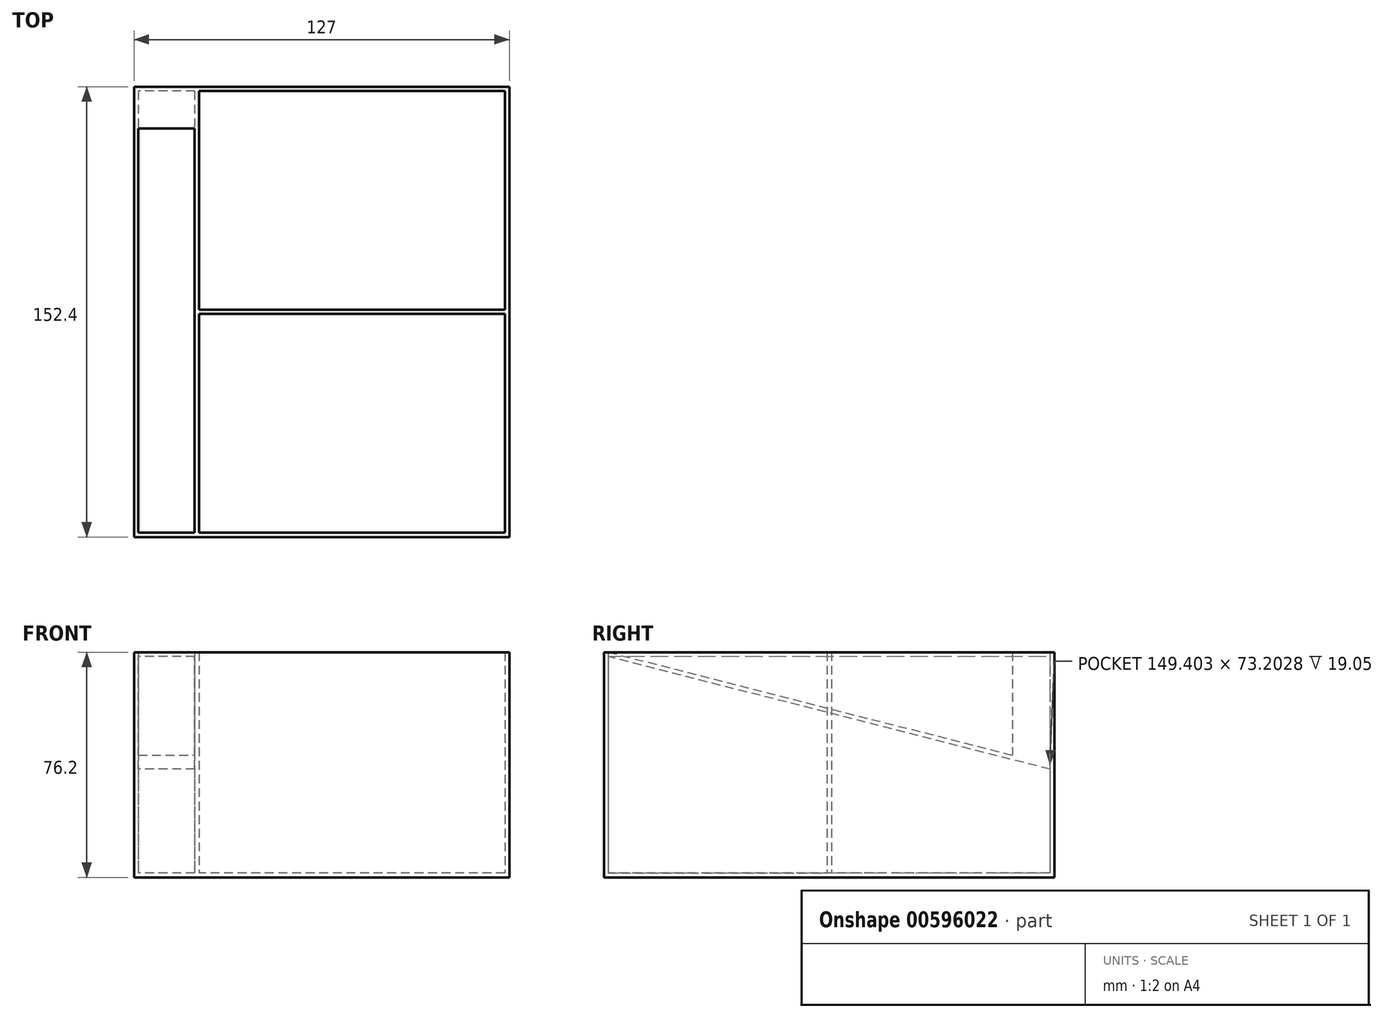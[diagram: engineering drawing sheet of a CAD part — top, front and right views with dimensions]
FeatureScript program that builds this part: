
annotation { "Feature Type Name" : "Feature", "Feature Type Description" : "" }
export const myFeature = defineFeature(function(context is Context, id is Id, definition is map)
    precondition{}
    {
        {
            var Q0;
            Q0=qCreatedBy(makeId("Top.planeOp"),FACE);
            var sketch = newSketch(context, id + "F0", { "sketchPlane" : qUnion([Q0])});
            skLineSegment(sketch, "E0.bottom", {"start": v(63.5, -76.2) * mm, "end": v(-63.5, -76.2) * mm});
            skLineSegment(sketch, "E0.top", {"start": v(63.5, 76.2) * mm, "end": v(-63.5, 76.2) * mm});
            skLineSegment(sketch, "E0.left", {"start": v(63.5, -76.2) * mm, "end": v(63.5, 76.2) * mm});
            skLineSegment(sketch, "E0.right", {"start": v(-63.5, -76.2) * mm, "end": v(-63.5, 76.2) * mm});
            skPoint(sketch, "E0.middle", {"position": v(0, 0) * mm});
            skSolve(sketch);
        }
        {
            var Q0;
            Q0=makeQuery(id+"F0.imprint","IMPRINT",FACE,{"disambiguationData":[TD([[makeQuery(id+"F0.imprint","IMPRINT",EDGE,{"derivedFrom":sQuery(id+"F0.wireOp",EDGE,"E0.bottom")}),-1.0]])]});
            extrude(context, id + "F1", {"entities" : qUnion([Q0]), "depth" : 76.2 * mm, "offsetDistance" : 25.4 * mm});
        }
        {
            var Q0;
            Q0=makeQuery(id+"F1.opExtrude","CAP_FACE",FACE,{"disambiguationData":[OSD([sQuery(id+"F0.wireOp",EDGE,"E0.bottom"),sQuery(id+"F0.wireOp",EDGE,"E0.top"),sQuery(id+"F0.wireOp",EDGE,"E0.left"),sQuery(id+"F0.wireOp",EDGE,"E0.right")])],"isStart":false});
            shell(context, id + "F2", {"entities" : qUnion([Q0]), "thickness" : 1.5 * mm});
        }
        {
            var Q0;
            Q0=makeQuery(id+"F2.opShell","OFFSET_FACE",FACE,{"disambiguationData":[OSD([sQuery(id+"F0.wireOp",EDGE,"E0.bottom"),sQuery(id+"F0.wireOp",EDGE,"E0.top"),sQuery(id+"F0.wireOp",EDGE,"E0.left"),sQuery(id+"F0.wireOp",EDGE,"E0.right")])]});
            var sketch = newSketch(context, id + "F3", { "sketchPlane" : qUnion([Q0])});
            skLineSegment(sketch, "E1.bottom", {"start": v(-42.95, 74.7) * mm, "end": v(-41.45, 74.7) * mm});
            skLineSegment(sketch, "E1.top", {"start": v(-42.95, -74.7) * mm, "end": v(-41.45, -74.7) * mm});
            skLineSegment(sketch, "E1.left", {"start": v(-42.95, 74.7) * mm, "end": v(-42.95, -74.7) * mm});
            skLineSegment(sketch, "E1.right", {"start": v(-41.45, 74.7) * mm, "end": v(-41.45, -74.7) * mm});
            skSolve(sketch);
        }
        {
            var Q0;
            Q0=makeQuery(id+"F2.opShell","OFFSET_FACE",FACE,{"disambiguationData":[OSD([sQuery(id+"F0.wireOp",EDGE,"E0.right")])]});
            var sketch = newSketch(context, id + "F4", { "sketchPlane" : qUnion([Q0])});
            skLineSegment(sketch, "E2", {"start": v(74.7, 36.6) * mm, "end": v(-74.7, 74.7) * mm});
            skLineSegment(sketch, "E3", {"start": v(-74.7, 74.7) * mm, "end": v(-74.7, 76.2) * mm});
            skLineSegment(sketch, "E4", {"start": v(-74.7, 76.2) * mm, "end": v(74.7, 38.1) * mm});
            skLineSegment(sketch, "E5", {"start": v(74.7, 38.1) * mm, "end": v(74.7, 36.6) * mm});
            skSolve(sketch);
        }
        {
            var Q0;
            Q0 = qSketchRegion(id + "F3", true);
            var Q1;
            {var subQ0=sQuery(id+"F0.wireOp",EDGE,"E0.right");var subQ1=sQuery(id+"F0.wireOp",EDGE,"E0.top");Q1=makeQuery(id+"F2.opShell","OFFSET_VERTEX",VERTEX,{"disambiguationData":[OSD([subQ1,subQ0]),TDD([makeQuery(id+"F1.opExtrude","CAP_VERTEX",VERTEX,{"disambiguationData":[OSD([subQ1,subQ0])],"isStart":false})])]});}
            extrude(context, id + "F5", {"entities" : qUnion([Q0]), "operationType" : NewBodyOperationType.ADD, "endBound" : BoundingType.UP_TO_VERTEX, "depth" : 73.66 * mm, "endBoundEntityVertex" : qUnion([Q1]), "offsetDistance" : 25.4 * mm});
        }
        {
            var Q0;
            Q0 = qSketchRegion(id + "F4", true);
            var Q1;
            Q1=makeQuery(id+"F1.opExtrude","SWEPT_BODY",BODY,{"disambiguationData":[OSD([sQuery(id+"F0.wireOp",EDGE,"E0.bottom"),sQuery(id+"F0.wireOp",EDGE,"E0.top"),sQuery(id+"F0.wireOp",EDGE,"E0.left"),sQuery(id+"F0.wireOp",EDGE,"E0.right")])]});
            extrude(context, id + "F6", {"entities" : qUnion([Q0]), "operationType" : NewBodyOperationType.ADD, "endBound" : BoundingType.UP_TO_BODY, "depth" : 25.4 * mm, "endBoundEntityBody" : qUnion([Q1]), "offsetDistance" : 25.4 * mm});
        }
        {
            var Q0;
            {var subQ0=sQuery(id+"F0.wireOp",EDGE,"E0.top");Q0=makeQuery(id+"F6.boolean.opBoolean","SPLIT",FACE,{"disambiguationData":[TD([makeQuery(id+"F1.opExtrude","CAP_FACE",FACE,{"disambiguationData":[OSD([sQuery(id+"F0.wireOp",EDGE,"E0.bottom"),subQ0,sQuery(id+"F0.wireOp",EDGE,"E0.left"),sQuery(id+"F0.wireOp",EDGE,"E0.right")])],"isStart":false})])],"derivedFrom":makeQuery(id+"F5.opExtrude","SWEPT_FACE",FACE,{"disambiguationData":[OSD([sQuery(id+"F3.wireOp",EDGE,"E1.left")])]})});}
            var sketch = newSketch(context, id + "F7", { "sketchPlane" : qUnion([Q0])});
            skLineSegment(sketch, "E6", {"start": v(-74.7, 38.1) * mm, "end": v(-74.7, 76.2) * mm});
            skLineSegment(sketch, "E7", {"start": v(-74.7, 76.2) * mm, "end": v(-62, 76.2) * mm});
            skLineSegment(sketch, "E8", {"start": v(-62, 76.2) * mm, "end": v(-62, 41.34) * mm});
            skLineSegment(sketch, "E9", {"start": v(-62, 41.34) * mm, "end": v(-74.7, 38.1) * mm});
            skSolve(sketch);
        }
        {
            var Q0;
            Q0=makeQuery(id+"F7.imprint","IMPRINT",FACE,{"disambiguationData":[TD([[makeQuery(id+"F7.imprint","IMPRINT",EDGE,{"derivedFrom":sQuery(id+"F7.wireOp",EDGE,"E6")}),1.0]])]});
            var Q1;
            {var subQ0=sQuery(id+"F0.wireOp",EDGE,"E0.right");var subQ1=sQuery(id+"F0.wireOp",EDGE,"E0.top");Q1=makeQuery(id+"F6.boolean.opBoolean","SPLIT",FACE,{"disambiguationData":[TD([makeQuery(id+"F1.opExtrude","CAP_FACE",FACE,{"disambiguationData":[OSD([sQuery(id+"F0.wireOp",EDGE,"E0.bottom"),subQ1,sQuery(id+"F0.wireOp",EDGE,"E0.left"),subQ0])],"isStart":false})])],"derivedFrom":makeQuery(id+"F2.opShell","OFFSET_FACE",FACE,{"disambiguationData":[OSD([subQ0])]})});}
            extrude(context, id + "F8", {"entities" : qUnion([Q0]), "operationType" : NewBodyOperationType.ADD, "endBound" : BoundingType.UP_TO_SURFACE, "depth" : 25.4 * mm, "endBoundEntityFace" : qUnion([Q1]), "offsetDistance" : 25.4 * mm});
        }
        {
            var Q0;
            {var subQ0=sQuery(id+"F0.wireOp",EDGE,"E0.bottom");var subQ1=sQuery(id+"F0.wireOp",EDGE,"E0.top");var subQ2=sQuery(id+"F0.wireOp",EDGE,"E0.left");Q0=makeQuery(id+"F5.boolean.opBoolean","SPLIT",FACE,{"disambiguationData":[TD([makeQuery(id+"F2.opShell","OFFSET_FACE",FACE,{"disambiguationData":[OSD([subQ2])]})])],"derivedFrom":makeQuery(id+"F2.opShell","OFFSET_FACE",FACE,{"disambiguationData":[OSD([subQ0,subQ1,subQ2,sQuery(id+"F0.wireOp",EDGE,"E0.right")])]})});}
            var sketch = newSketch(context, id + "F9", { "sketchPlane" : qUnion([Q0])});
            skLineSegment(sketch, "E10", {"start": v(10.27, 74.7) * mm, "end": v(10.27, -74.7) * mm, "construction": true});
            skLineSegment(sketch, "E11", {"start": v(62, 0) * mm, "end": v(-41.45, 0) * mm, "construction": true});
            skLineSegment(sketch, "E12.bottom", {"start": v(62, -0.75) * mm, "end": v(-41.45, -0.75) * mm});
            skLineSegment(sketch, "E12.top", {"start": v(62, 0.75) * mm, "end": v(-41.45, 0.75) * mm});
            skLineSegment(sketch, "E12.left", {"start": v(62, -0.75) * mm, "end": v(62, 0.75) * mm});
            skLineSegment(sketch, "E12.right", {"start": v(-41.45, -0.75) * mm, "end": v(-41.45, 0.75) * mm});
            skPoint(sketch, "E12.middle", {"position": v(10.27, 0) * mm});
            skSolve(sketch);
        }
        {
            var Q0;
            Q0 = qSketchRegion(id + "F9", true);
            var Q1;
            Q1=makeQuery(id+"F1.opExtrude","SWEPT_BODY",BODY,{"disambiguationData":[OSD([sQuery(id+"F0.wireOp",EDGE,"E0.bottom"),sQuery(id+"F0.wireOp",EDGE,"E0.top"),sQuery(id+"F0.wireOp",EDGE,"E0.left"),sQuery(id+"F0.wireOp",EDGE,"E0.right")])]});
            var Q2;
            Q2=makeQuery(id+"F5.opExtrude","CAP_VERTEX",VERTEX,{"disambiguationData":[OSD([sQuery(id+"F0.wireOp",EDGE,"E0.bottom"),sQuery(id+"F3.wireOp",EDGE,"E1.top"),sQuery(id+"F3.wireOp",EDGE,"E1.right"),dummyQuery(id+"F5.vertexPlane.planeOp",FACE)])],"isStart":false});
            extrude(context, id + "F10", {"entities" : qUnion([Q0]), "operationType" : NewBodyOperationType.ADD, "endBound" : BoundingType.UP_TO_VERTEX, "depth" : 25.4 * mm, "endBoundEntityBody" : qUnion([Q1]), "endBoundEntityVertex" : qUnion([Q2]), "offsetDistance" : 25.4 * mm});
        }
    });
